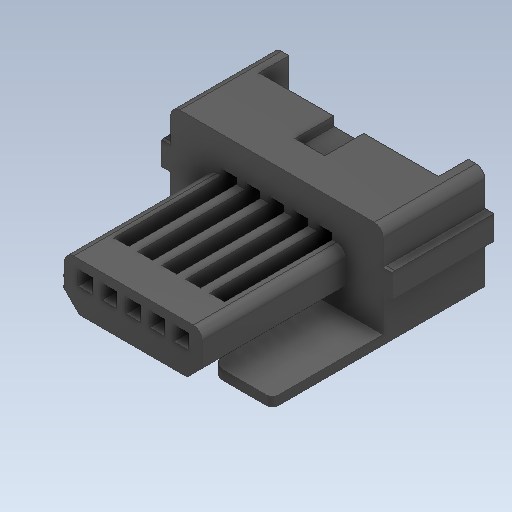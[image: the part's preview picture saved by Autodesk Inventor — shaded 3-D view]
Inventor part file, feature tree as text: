
AUTODESK INVENTOR PART (.ipt)
format: ipt  version: 2020 (Build 240168000, 168)  size: 216,576 bytes
history: native  units: in
note: dims shown in document units (in); Inventor stores cm internally (conversion verified against a paired STEP export)
features: fillet x1
ambient origin geometry x8: Origin, YZ Plane, XZ Plane, XY Plane, X Axis, Y Axis, Z Axis, Center Point
bodies: Solid1 (feature_tree)
feature tree (1):
  fillet  "Fillet3"  [1 undecoded]
note: 1 required parameter value undecoded (feature->parameter linkage not recoverable at this tier; creation-order binding heuristic only, values carry confidence <= 0.55)
